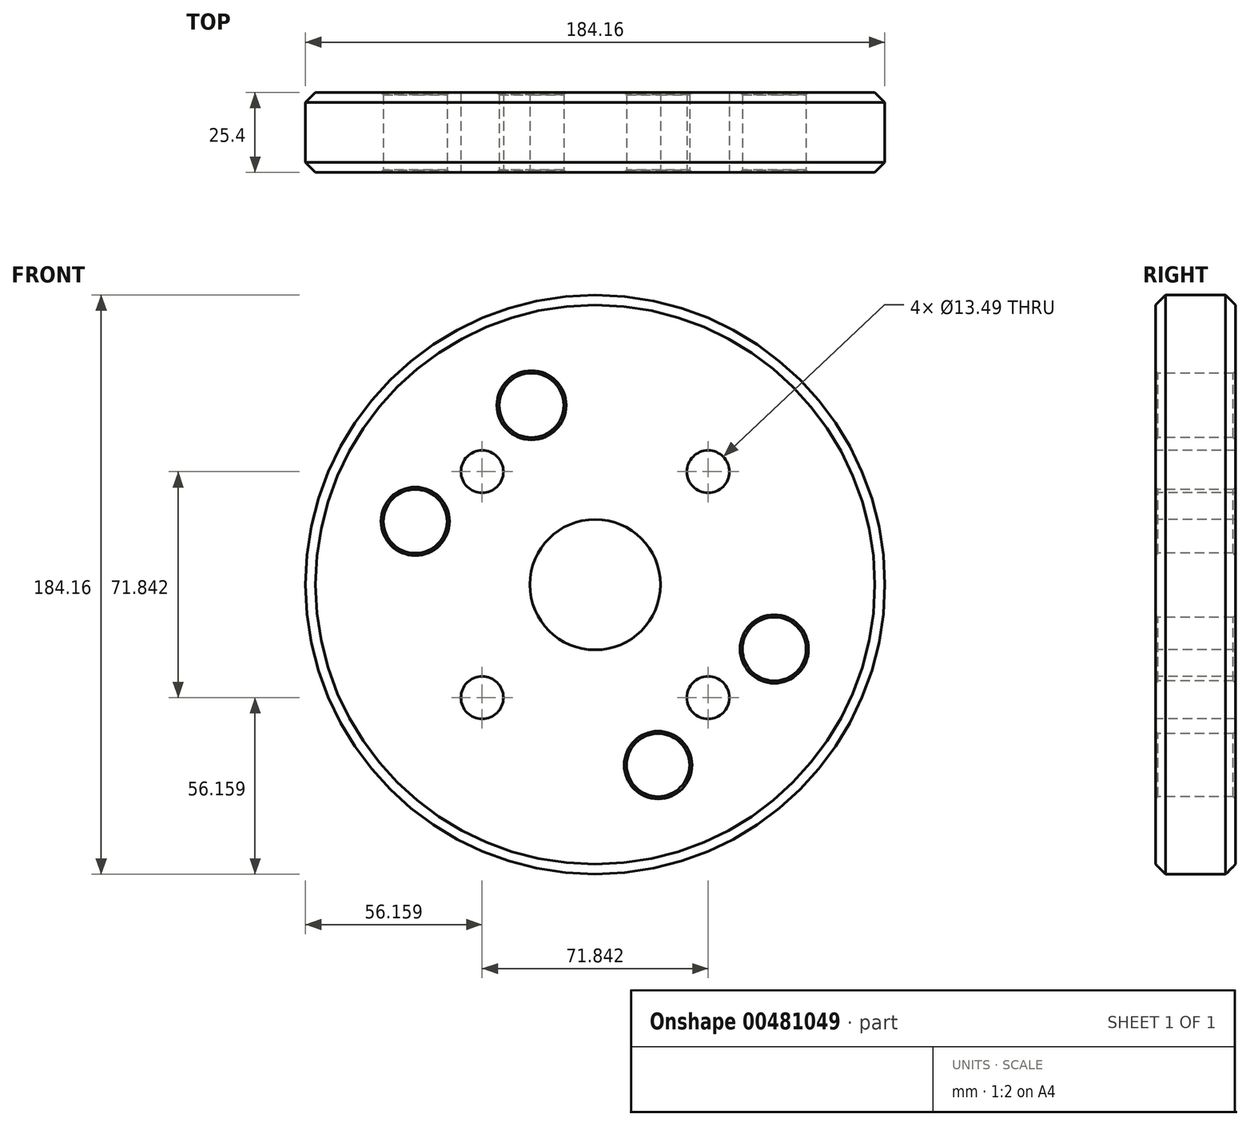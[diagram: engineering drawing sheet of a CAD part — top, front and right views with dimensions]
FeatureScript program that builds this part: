
annotation { "Feature Type Name" : "Feature", "Feature Type Description" : "" }
export const myFeature = defineFeature(function(context is Context, id is Id, definition is map)
    precondition{}
    {
        {
            var Q0;
            Q0=qCreatedBy(makeId("Front.planeOp"),FACE);
            var sketch = newSketch(context, id + "F0", { "sketchPlane" : qUnion([Q0])});
            skCircle(sketch, "E0", {"center": v(0, 0) * mm, "radius": 92.08 * mm});
            skCircle(sketch, "E1", {"center": v(0, 0) * mm, "radius": 20.75 * mm});
            skSolve(sketch);
        }
        {
            var Q0;
            Q0=qSketchRegion(id+"F0",true);
            extrude(context, id + "F1", {"entities" : qUnion([Q0]), "oppositeDirection" : true, "depth" : 25.4 * mm});
        }
        {
            var Q0;
            Q0=makeQuery(id+"F1.opExtrude","CAP_FACE",FACE,{"disambiguationData":[OSD([sQuery(id+"F0.wireOp",EDGE,"E0"),sQuery(id+"F0.wireOp",EDGE,"E1")])],"isStart":true});
            var sketch = newSketch(context, id + "F2", { "sketchPlane" : qUnion([Q0])});
            skLineSegment(sketch, "E2", {"start": v(0, 92.08) * mm, "end": v(0, -92.08) * mm, "construction": true});
            skLineSegment(sketch, "E3.0", {"start": v(-10, 92.08) * mm, "end": v(-10, -92.08) * mm, "construction": true});
            skCircle(sketch, "E4", {"center": v(0, 0) * mm, "radius": 70.75 * mm, "construction": true});
            skCircle(sketch, "E5", {"center": v(0, 0) * mm, "radius": 30.64 * mm, "construction": true});
            skCircle(sketch, "E6", {"center": v(-20.25, 57.01) * mm, "radius": 10.25 * mm, "construction": true});
            skCircle(sketch, "E7", {"center": v(-20.25, 57.01) * mm, "radius": 10.25 * mm});
            skLineSegment(sketch, "E8", {"start": v(0, 0) * mm, "end": v(-99.85, 0) * mm, "construction": true});
            skLineSegment(sketch, "E9.0", {"start": v(0, 10) * mm, "end": v(-99.85, 10) * mm, "construction": true});
            skCircle(sketch, "E10", {"center": v(-57.19, 20.13) * mm, "radius": 10.13 * mm});
            skCircle(sketch, "E11.1.0", {"center": v(56.94, -20.48) * mm, "radius": 10.13 * mm});
            skCircle(sketch, "E11.1.1", {"center": v(20, -57.36) * mm, "radius": 10.25 * mm, "construction": true});
            skPoint(sketch, "E11.center", {"position": v(-0.13, -0.18) * mm});
            skCircle(sketch, "E12", {"center": v(20, -57.36) * mm, "radius": 10 * mm});
            skSolve(sketch);
        }
        {
            var Q0;
            Q0=makeQuery(id+"F2.imprint","IMPRINT",FACE,{"disambiguationData":[TD([[makeQuery(id+"F2.imprint","IMPRINT",EDGE,{"derivedFrom":sQuery(id+"F2.wireOp",EDGE,"E10")}),1.0]])]});
            var Q1;
            Q1=makeQuery(id+"F2.imprint","IMPRINT",FACE,{"disambiguationData":[TD([[makeQuery(id+"F2.imprint","IMPRINT",EDGE,{"derivedFrom":sQuery(id+"F2.wireOp",EDGE,"E7")}),1.0]])]});
            var Q2;
            Q2=makeQuery(id+"F2.imprint","IMPRINT",FACE,{"disambiguationData":[TD([[makeQuery(id+"F2.imprint","IMPRINT",EDGE,{"derivedFrom":sQuery(id+"F2.wireOp",EDGE,"E11.1.0")}),1.0]])]});
            var Q3;
            Q3=makeQuery(id+"F2.imprint","IMPRINT",FACE,{"disambiguationData":[TD([[makeQuery(id+"F2.imprint","IMPRINT",EDGE,{"derivedFrom":sQuery(id+"F2.wireOp",EDGE,"E12")}),1.0]])]});
            extrude(context, id + "F3", {"entities" : qUnion([Q0, Q1, Q2, Q3]), "operationType" : NewBodyOperationType.REMOVE, "oppositeDirection" : true, "depth" : 25.4 * mm});
        }
        {
            var Q0;
            Q0=makeQuery(id+"F1.opExtrude","CAP_FACE",FACE,{"disambiguationData":[OSD([sQuery(id+"F0.wireOp",EDGE,"E0"),sQuery(id+"F0.wireOp",EDGE,"E1")])],"isStart":true});
            var sketch = newSketch(context, id + "F4", { "sketchPlane" : qUnion([Q0])});
            skCircle(sketch, "E13", {"center": v(0, 0) * mm, "radius": 50.8 * mm, "construction": true});
            skLineSegment(sketch, "E14", {"start": v(0, 0) * mm, "end": v(-35.92, 35.92) * mm, "construction": true});
            skPoint(sketch, "E15", {"position": v(-35.92, 35.92) * mm});
            skPoint(sketch, "E16.1.0", {"position": v(-35.92, -35.92) * mm});
            skPoint(sketch, "E16.2.0", {"position": v(35.92, -35.92) * mm});
            skPoint(sketch, "E16.3.0", {"position": v(35.92, 35.92) * mm});
            skSolve(sketch);
        }
        {
            var Q0;
            Q0=sQuery(id+"F4.wireOp",VERTEX,"E15");
            var Q1;
            Q1=sQuery(id+"F4.wireOp",VERTEX,"E16.3.0");
            var Q2;
            Q2=sQuery(id+"F4.wireOp",VERTEX,"E16.2.0");
            var Q3;
            Q3=sQuery(id+"F4.wireOp",VERTEX,"E16.1.0");
            var Q4;
            Q4=makeQuery(id+"F1.opExtrude","SWEPT_BODY",BODY,{"disambiguationData":[OSD([sQuery(id+"F0.wireOp",EDGE,"E0"),sQuery(id+"F0.wireOp",EDGE,"E1")])]});
            hole(context, id + "F5", {"style" : HoleStyle.SIMPLE, "endStyle" : HoleEndStyle.THROUGH, "standardTappedOrClearance" : lookupTablePath({ "standard" : "ANSI", "fit" : "Normal (ASME)", "size" : "1/2", "type" : "Clearance" }), "standardBlindInLast" : lookupTablePath({ "fit" : "Free", "standard" : "ANSI", "size" : "1/2", "type" : "Clearance" }), "holeDiameter" : 13.5 * mm, "tappedDepth" : 15.88 * mm, "tapClearance" : 3, "startFromSketch" : true, "locations" : qUnion([Q0, Q1, Q2, Q3]), "scope" : qUnion([Q4])});
        }
        {
            var Q0;
            Q0=makeQuery(id+"F1.opExtrude","SWEPT_FACE",FACE,{"disambiguationData":[OSD([sQuery(id+"F0.wireOp",EDGE,"E0")])]});
            chamfer(context, id + "F6", {"entities" : qUnion([Q0]), "width" : 3.17 * mm, "tangentPropagation" : true});
        }
        {
            var Q0;
            Q0=makeQuery(id+"F3.boolean.opBoolean","COPY",FACE,{"derivedFrom":makeQuery(id+"F3.opExtrude","SWEPT_FACE",FACE,{"disambiguationData":[OSD([sQuery(id+"F2.wireOp",EDGE,"E10")])]})});
            var Q1;
            Q1=makeQuery(id+"F3.boolean.opBoolean","COPY",FACE,{"derivedFrom":makeQuery(id+"F3.opExtrude","SWEPT_FACE",FACE,{"disambiguationData":[OSD([sQuery(id+"F2.wireOp",EDGE,"E7")])]})});
            var Q2;
            Q2=makeQuery(id+"F5.hole-1.boolean.opBoolean","COPY",FACE,{"derivedFrom":makeQuery(id+"F5.hole-1.opRevolve","SWEPT_FACE",FACE,{"disambiguationData":[OSD([sQuery(id+"F5.hole-1.sketch.wireOp",EDGE,"core_line_2")])]})});
            var Q3;
            Q3=makeQuery(id+"F3.boolean.opBoolean","COPY",FACE,{"derivedFrom":makeQuery(id+"F3.opExtrude","SWEPT_FACE",FACE,{"disambiguationData":[OSD([sQuery(id+"F2.wireOp",EDGE,"E11.1.0")])]})});
            var Q4;
            Q4=makeQuery(id+"F3.boolean.opBoolean","COPY",FACE,{"derivedFrom":makeQuery(id+"F3.opExtrude","SWEPT_FACE",FACE,{"disambiguationData":[OSD([sQuery(id+"F2.wireOp",EDGE,"E12")])]})});
            var Q5;
            Q5=makeQuery(id+"F5.hole-3.boolean.opBoolean","COPY",FACE,{"derivedFrom":makeQuery(id+"F5.hole-3.opRevolve","SWEPT_FACE",FACE,{"disambiguationData":[OSD([sQuery(id+"F5.hole-3.sketch.wireOp",EDGE,"core_line_2")])]})});
            var Q6;
            Q6=makeQuery(id+"F5.hole-2.boolean.opBoolean","COPY",FACE,{"derivedFrom":makeQuery(id+"F5.hole-2.opRevolve","SWEPT_FACE",FACE,{"disambiguationData":[OSD([sQuery(id+"F5.hole-2.sketch.wireOp",EDGE,"core_line_2")])]})});
            var Q7;
            Q7=makeQuery(id+"F5.hole-0.boolean.opBoolean","COPY",FACE,{"derivedFrom":makeQuery(id+"F5.hole-0.opRevolve","SWEPT_FACE",FACE,{"disambiguationData":[OSD([sQuery(id+"F5.hole-0.sketch.wireOp",EDGE,"core_line_2")])]})});
            chamfer(context, id + "F7", {"entities" : qUnion([Q0, Q1, Q2, Q3, Q4, Q5, Q6, Q7]), "width" : 0.76 * mm, "tangentPropagation" : true});
        }
    });
